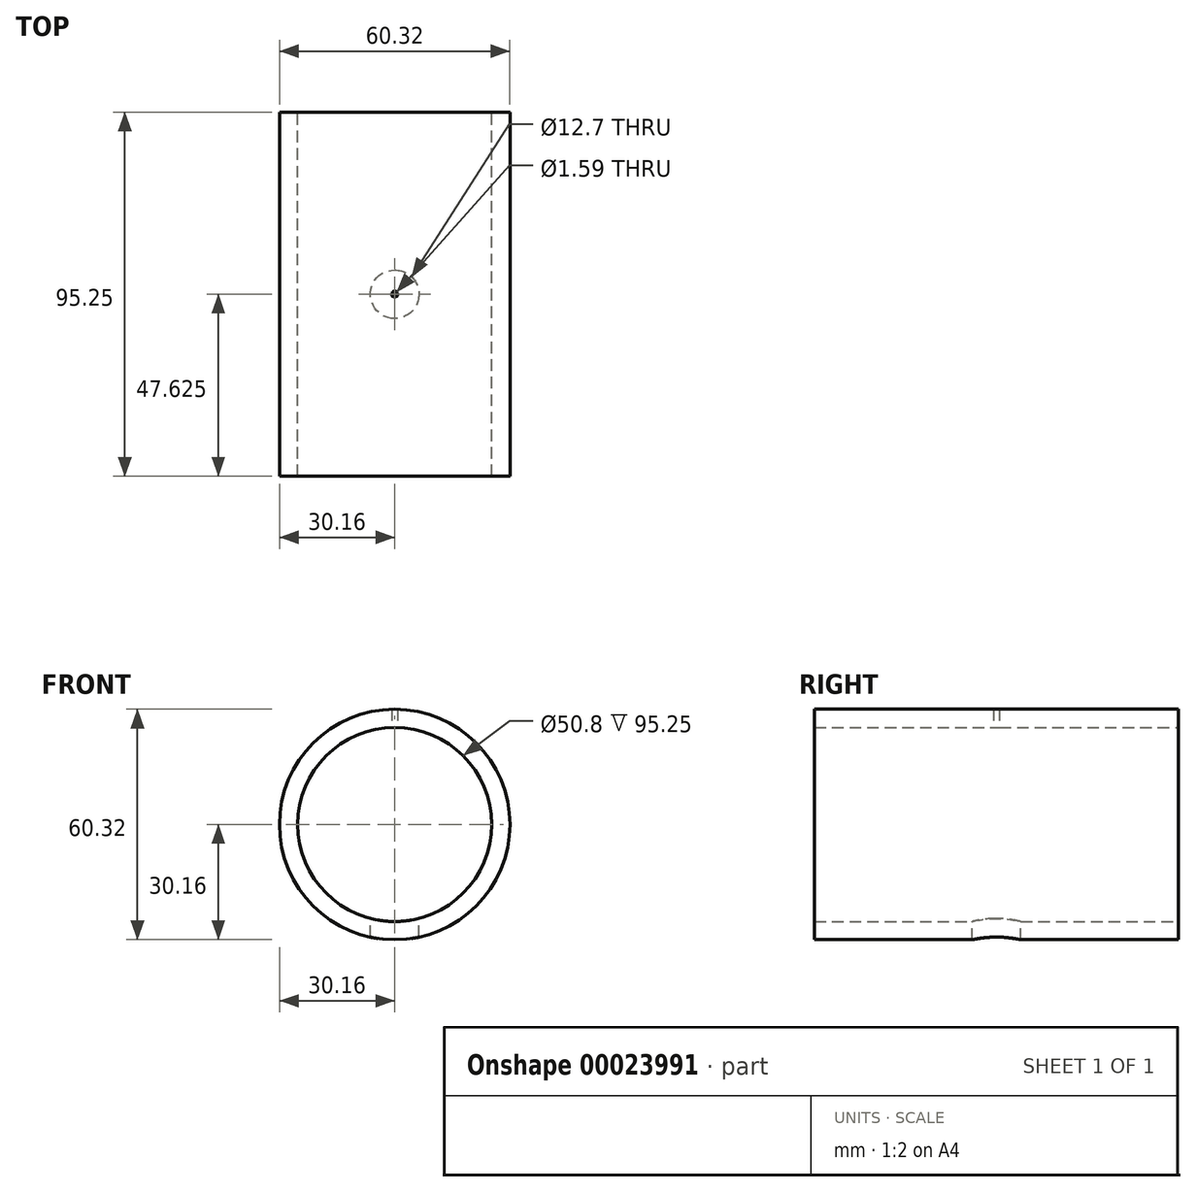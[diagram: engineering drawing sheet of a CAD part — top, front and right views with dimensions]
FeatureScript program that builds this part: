
annotation { "Feature Type Name" : "Feature", "Feature Type Description" : "" }
export const myFeature = defineFeature(function(context is Context, id is Id, definition is map)
    precondition{}
    {
        {
            var Q0;
            Q0=qCreatedBy(makeId("Front.planeOp"),FACE);
            var sketch = newSketch(context, id + "F0", { "sketchPlane" : qUnion([Q0])});
            skCircle(sketch, "E0", {"center": v(0, 0) * mm, "radius": 25.4 * mm});
            skCircle(sketch, "E1", {"center": v(0, 0) * mm, "radius": 30.16 * mm});
            skLineSegment(sketch, "E2", {"start": v(0, 30.16) * mm, "end": v(0, 10.05) * mm});
            skSolve(sketch);
        }
        {
            var Q0;
            Q0 = qSketchRegion(id + "F0", true);
            extrude(context, id + "F1", {"entities" : qUnion([Q0]), "depth" : 95.25 * mm});
        }
        {
            var Q0;
            Q0=qCreatedBy(makeId("Top.planeOp"),FACE);
            var sketch = newSketch(context, id + "F2", { "sketchPlane" : qUnion([Q0])});
            skPoint(sketch, "E3", {"position": v(0, -47.63) * mm});
            skSolve(sketch);
        }
        {
            var Q0;
            Q0=sQuery(id+"F2.wireOp",VERTEX,"E3");
            var Q1;
            Q1=makeQuery(id+"F1.opExtrude","SWEPT_BODY",BODY,{"disambiguationData":[OSD([sQuery(id+"F0.wireOp",EDGE,"E0"),sQuery(id+"F0.wireOp",EDGE,"E1")])]});
            hole(context, id + "F3", {"style" : HoleStyle.SIMPLE, "holeDiameter" : 12.7 * mm, "endStyle" : HoleEndStyle.THROUGH, "locations" : qUnion([Q0]), "scope" : qUnion([Q1])});
        }
        {
            var Q0;
            Q0=qCreatedBy(makeId("Top.planeOp"),FACE);
            var sketch = newSketch(context, id + "F4", { "sketchPlane" : qUnion([Q0])});
            skPoint(sketch, "E4", {"position": v(0, -47.63) * mm});
            skSolve(sketch);
        }
        {
            var Q0;
            Q0=sQuery(id+"F4.wireOp",VERTEX,"E4");
            var Q1;
            Q1=makeQuery(id+"F1.opExtrude","SWEPT_BODY",BODY,{"disambiguationData":[OSD([sQuery(id+"F0.wireOp",EDGE,"E0"),sQuery(id+"F0.wireOp",EDGE,"E1")])]});
            hole(context, id + "F5", {"style" : HoleStyle.SIMPLE, "holeDiameter" : 1.59 * mm, "endStyle" : HoleEndStyle.THROUGH, "oppositeDirection" : true, "locations" : qUnion([Q0]), "scope" : qUnion([Q1])});
        }
    });
